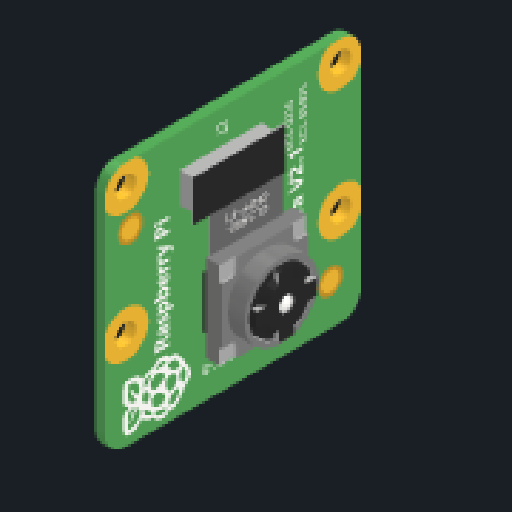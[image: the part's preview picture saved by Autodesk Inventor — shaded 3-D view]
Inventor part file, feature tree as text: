
AUTODESK INVENTOR PART (.ipt)
format: ipt  version: 2023 (Build 270158000, 158)  size: 2,803,712 bytes
history: native  units: mm
features: sketch x3, other x2, plane x2, projected_geometry x1
ambient origin geometry x8: Origin, YZ Plane, XZ Plane, XY Plane, X Axis, Y Axis, Z Axis, Center Point
bodies: Solid1 (feature_tree), Body1 (feature_tree)
feature tree (8):
  other  "Decal1"
  plane  "Work Plane1"
  sketch  "Sketch2"  dims[d52=75.0mm]
  plane  "Work Plane2"
  sketch  "Sketch3"  dims[d54=4.258603mm d55=5.427974mm]
  sketch  "Sketch1"  dims[d45=0.0mm]
  other  "Image1"
  projected_geometry  "Projected Loop1"
